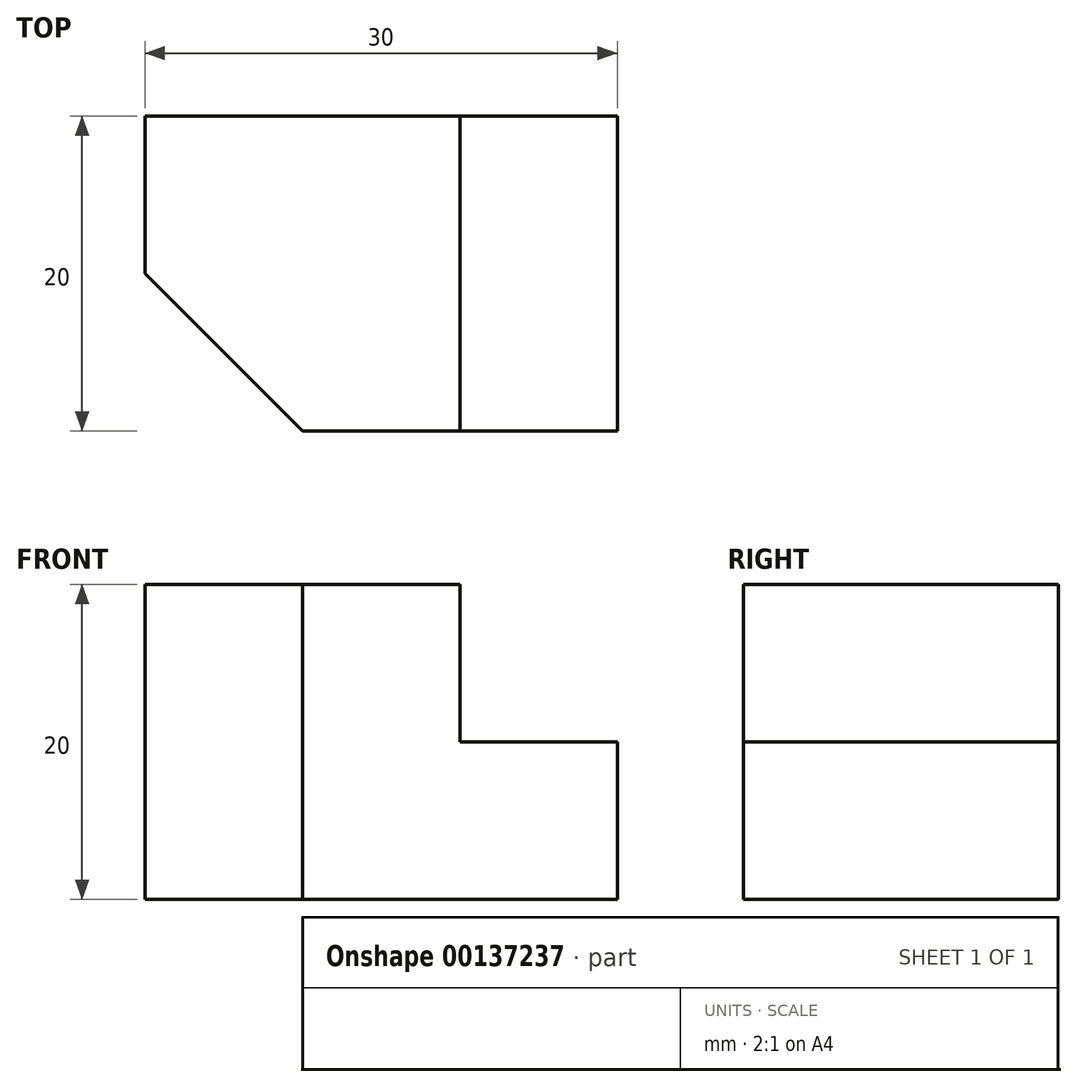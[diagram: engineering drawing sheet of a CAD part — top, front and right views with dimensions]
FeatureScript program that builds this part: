
annotation { "Feature Type Name" : "Feature", "Feature Type Description" : "" }
export const myFeature = defineFeature(function(context is Context, id is Id, definition is map)
    precondition{}
    {
        {
            var Q0;
            Q0=qCreatedBy(makeId("Top.planeOp"),FACE);
            var sketch = newSketch(context, id + "F0", { "sketchPlane" : qUnion([Q0])});
            skLineSegment(sketch, "E0.bottom", {"start": v(0, 0) * mm, "end": v(30, 0) * mm});
            skLineSegment(sketch, "E0.top", {"start": v(0, 20) * mm, "end": v(30, 20) * mm});
            skLineSegment(sketch, "E0.left", {"start": v(0, 0) * mm, "end": v(0, 20) * mm});
            skLineSegment(sketch, "E0.right", {"start": v(30, 0) * mm, "end": v(30, 20) * mm});
            skSolve(sketch);
        }
        {
            var Q0;
            Q0 = qSketchRegion(id + "F0", true);
            extrude(context, id + "F1", {"entities" : qUnion([Q0]), "depth" : 20 * mm});
        }
        {
            var Q0;
            Q0=makeQuery(id+"F1.opExtrude","CAP_FACE",FACE,{"disambiguationData":[OSD([sQuery(id+"F0.wireOp",EDGE,"E0.bottom"),sQuery(id+"F0.wireOp",EDGE,"E0.top"),sQuery(id+"F0.wireOp",EDGE,"E0.left"),sQuery(id+"F0.wireOp",EDGE,"E0.right")])],"isStart":false});
            var sketch = newSketch(context, id + "F2", { "sketchPlane" : qUnion([Q0])});
            skLineSegment(sketch, "E1", {"start": v(0, 0) * mm, "end": v(0, 10) * mm});
            skLineSegment(sketch, "E2", {"start": v(0, 10) * mm, "end": v(10, 0) * mm});
            skLineSegment(sketch, "E3", {"start": v(10, 0) * mm, "end": v(0, 0) * mm});
            skSolve(sketch);
        }
        {
            var Q0;
            Q0 = qSketchRegion(id + "F2", true);
            extrude(context, id + "F3", {"entities" : qUnion([Q0]), "operationType" : NewBodyOperationType.REMOVE, "endBound" : BoundingType.THROUGH_ALL, "oppositeDirection" : true, "depth" : 25 * mm});
        }
        {
            var Q0;
            Q0=makeQuery(id+"F1.opExtrude","SWEPT_FACE",FACE,{"disambiguationData":[OSD([sQuery(id+"F0.wireOp",EDGE,"E0.bottom")])]});
            var sketch = newSketch(context, id + "F4", { "sketchPlane" : qUnion([Q0])});
            skLineSegment(sketch, "E4.bottom", {"start": v(30, 20) * mm, "end": v(20, 20) * mm});
            skLineSegment(sketch, "E4.top", {"start": v(30, 10) * mm, "end": v(20, 10) * mm});
            skLineSegment(sketch, "E4.left", {"start": v(30, 20) * mm, "end": v(30, 10) * mm});
            skLineSegment(sketch, "E4.right", {"start": v(20, 20) * mm, "end": v(20, 10) * mm});
            skSolve(sketch);
        }
        {
            var Q0;
            Q0 = qSketchRegion(id + "F4", true);
            extrude(context, id + "F5", {"entities" : qUnion([Q0]), "operationType" : NewBodyOperationType.REMOVE, "endBound" : BoundingType.THROUGH_ALL, "oppositeDirection" : true, "depth" : 25 * mm});
        }
    });
